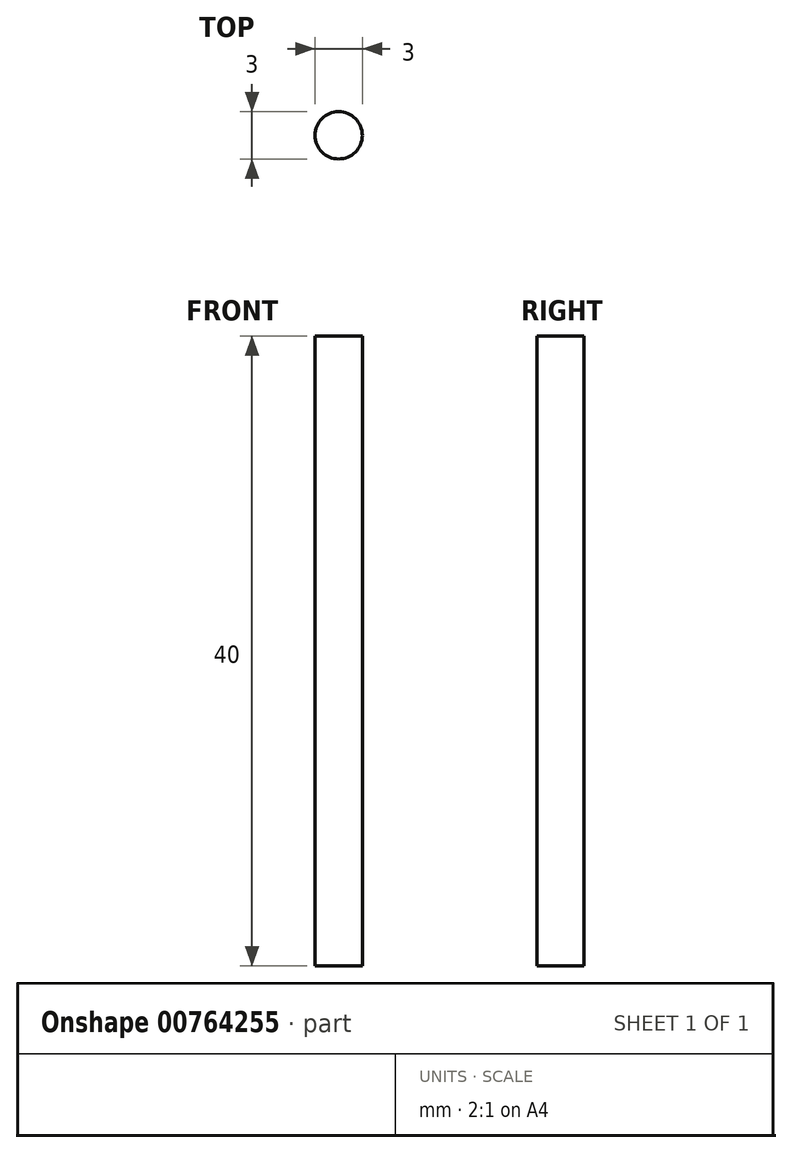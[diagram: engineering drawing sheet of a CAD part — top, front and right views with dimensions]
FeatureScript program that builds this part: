
annotation { "Feature Type Name" : "Feature", "Feature Type Description" : "" }
export const myFeature = defineFeature(function(context is Context, id is Id, definition is map)
    precondition{}
    {
        {
            var Q0;
            Q0=qCreatedBy(makeId("Top.planeOp"),FACE);
            var sketch = newSketch(context, id + "F0", { "sketchPlane" : qUnion([Q0])});
            skCircle(sketch, "E0", {"center": v(0, 0) * mm, "radius": 1.5 * mm});
            skSolve(sketch);
        }
        {
            var Q0;
            Q0 = qSketchRegion(id + "F0", true);
            extrude(context, id + "F1", {"entities" : qUnion([Q0]), "depth" : 40 * mm, "offsetDistance" : 25 * mm});
        }
    });
